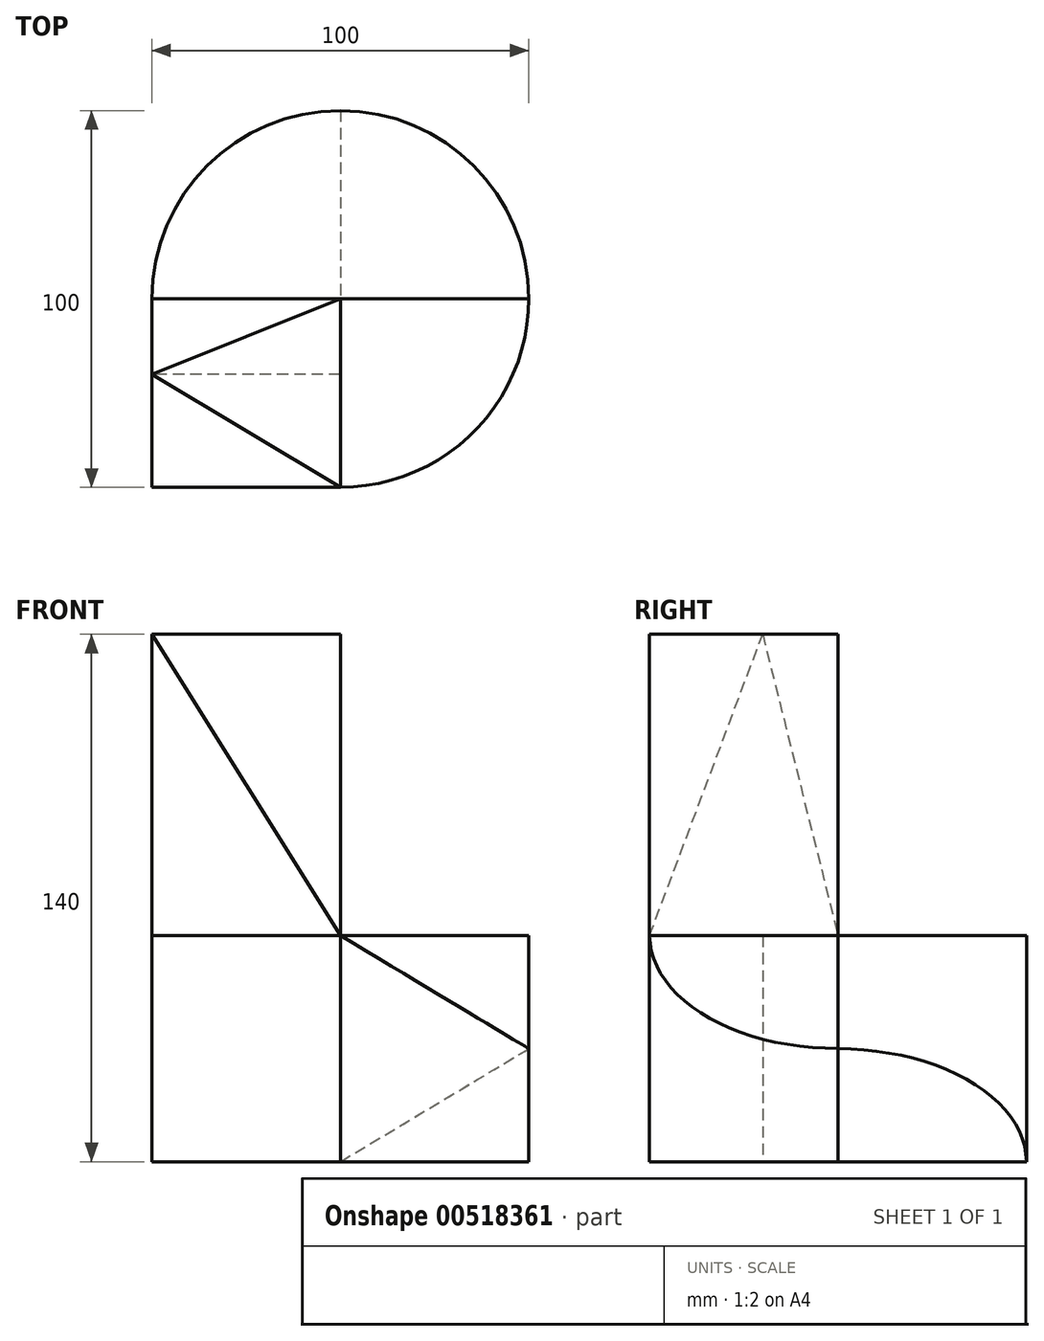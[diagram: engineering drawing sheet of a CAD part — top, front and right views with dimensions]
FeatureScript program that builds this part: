
annotation { "Feature Type Name" : "Feature", "Feature Type Description" : "" }
export const myFeature = defineFeature(function(context is Context, id is Id, definition is map)
    precondition{}
    {
        {
            var Q0;
            Q0=qCreatedBy(makeId("Top.planeOp"),FACE);
            var sketch = newSketch(context, id + "F0", { "sketchPlane" : qUnion([Q0])});
            skLineSegment(sketch, "E0.bottom", {"start": v(0, 0) * mm, "end": v(100, 0) * mm});
            skLineSegment(sketch, "E0.top", {"start": v(0, 100) * mm, "end": v(100, 100) * mm});
            skLineSegment(sketch, "E0.left", {"start": v(0, 0) * mm, "end": v(0, 100) * mm});
            skLineSegment(sketch, "E0.right", {"start": v(100, 0) * mm, "end": v(100, 100) * mm});
            skSolve(sketch);
        }
        {
            var Q0;
            Q0 = qSketchRegion(id + "F0", true);
            extrude(context, id + "F1", {"entities" : qUnion([Q0]), "depth" : 140 * mm, "offsetDistance" : 25 * mm});
        }
        {
            var Q0;
            Q0=makeQuery(id+"F1.opExtrude","CAP_FACE",FACE,{"disambiguationData":[OSD([sQuery(id+"F0.wireOp",EDGE,"E0.bottom"),sQuery(id+"F0.wireOp",EDGE,"E0.top"),sQuery(id+"F0.wireOp",EDGE,"E0.left"),sQuery(id+"F0.wireOp",EDGE,"E0.right")])],"isStart":false});
            var sketch = newSketch(context, id + "F2", { "sketchPlane" : qUnion([Q0])});
            skCircle(sketch, "E1", {"center": v(50, 50) * mm, "radius": 50 * mm});
            skSolve(sketch);
        }
        {
            var Q0;
            {var subQ0=sQuery(id+"F2.wireOp",EDGE,"E1");var subQ1=makeQuery(id+"F1.opExtrude","CAP_EDGE",EDGE,{"disambiguationData":[OSD([sQuery(id+"F0.wireOp",EDGE,"E0.top")])],"isStart":false});var subQ2=makeQuery(id+"F2.imprint","INTERSECT",VERTEX,{"derivedFrom":[subQ1,subQ0]});Q0=makeQuery(id+"F2.imprint","IMPRINT",FACE,{"disambiguationData":[TD([[makeQuery(id+"F2.imprint","IMPRINT",EDGE,{"disambiguationData":[TD([[subQ2,-1.0]])],"derivedFrom":subQ0}),-1.0]])]});}
            var Q1;
            {var subQ0=sQuery(id+"F2.wireOp",EDGE,"E1");var subQ1=makeQuery(id+"F1.opExtrude","CAP_EDGE",EDGE,{"disambiguationData":[OSD([sQuery(id+"F0.wireOp",EDGE,"E0.top")])],"isStart":false});var subQ2=makeQuery(id+"F2.imprint","INTERSECT",VERTEX,{"derivedFrom":[subQ1,subQ0]});Q1=makeQuery(id+"F2.imprint","IMPRINT",FACE,{"disambiguationData":[TD([[makeQuery(id+"F2.imprint","IMPRINT",EDGE,{"disambiguationData":[TD([[subQ2,1.0]])],"derivedFrom":subQ0}),-1.0]])]});}
            var Q2;
            {var subQ0=sQuery(id+"F2.wireOp",EDGE,"E1");var subQ1=makeQuery(id+"F1.opExtrude","CAP_EDGE",EDGE,{"disambiguationData":[OSD([sQuery(id+"F0.wireOp",EDGE,"E0.right")])],"isStart":false});var subQ2=makeQuery(id+"F2.imprint","INTERSECT",VERTEX,{"derivedFrom":[subQ1,subQ0]});Q2=makeQuery(id+"F2.imprint","IMPRINT",FACE,{"disambiguationData":[TD([[makeQuery(id+"F2.imprint","IMPRINT",EDGE,{"disambiguationData":[TD([[subQ2,1.0]])],"derivedFrom":subQ0}),-1.0]])]});}
            extrude(context, id + "F3", {"entities" : qUnion([Q0, Q1, Q2]), "operationType" : NewBodyOperationType.REMOVE, "endBound" : BoundingType.THROUGH_ALL, "oppositeDirection" : true, "depth" : 25 * mm, "offsetDistance" : 25 * mm});
        }
        {
            var Q0;
            Q0=makeQuery(id+"F1.opExtrude","CAP_FACE",FACE,{"disambiguationData":[OSD([sQuery(id+"F0.wireOp",EDGE,"E0.bottom"),sQuery(id+"F0.wireOp",EDGE,"E0.top"),sQuery(id+"F0.wireOp",EDGE,"E0.left"),sQuery(id+"F0.wireOp",EDGE,"E0.right")])],"isStart":false});
            var sketch = newSketch(context, id + "F4", { "sketchPlane" : qUnion([Q0])});
            skLineSegment(sketch, "E2", {"start": v(0, 50) * mm, "end": v(50, 50) * mm});
            skLineSegment(sketch, "E3", {"start": v(50, 50) * mm, "end": v(50, 0) * mm});
            skSolve(sketch);
        }
        {
            var Q0;
            Q0=makeQuery(id+"F4.imprint","IMPRINT",FACE,{"disambiguationData":[TD([[makeQuery(id+"F4.imprint","IMPRINT",EDGE,{"derivedFrom":sQuery(id+"F4.wireOp",EDGE,"E2")}),1.0]])]});
            extrude(context, id + "F5", {"entities" : qUnion([Q0]), "operationType" : NewBodyOperationType.REMOVE, "oppositeDirection" : true, "depth" : 80 * mm, "offsetDistance" : 25 * mm});
        }
        {
            var Q0;
            Q0=makeQuery(id+"F1.opExtrude","SWEPT_FACE",FACE,{"disambiguationData":[OSD([sQuery(id+"F0.wireOp",EDGE,"E0.bottom")])]});
            var sketch = newSketch(context, id + "F6", { "sketchPlane" : qUnion([Q0])});
            skLineSegment(sketch, "E4", {"start": v(50, 60) * mm, "end": v(0, 60) * mm});
            skLineSegment(sketch, "E5", {"start": v(0, 60) * mm, "end": v(0, 140) * mm});
            skLineSegment(sketch, "E6", {"start": v(0, 140) * mm, "end": v(50, 140) * mm});
            skLineSegment(sketch, "E7", {"start": v(50, 140) * mm, "end": v(50, 60) * mm});
            skSolve(sketch);
        }
        {
            var Q0;
            Q0=qCreatedBy(makeId("Front.planeOp"),FACE);
            var Q1;
            {var subQ0=sQuery(id+"F4.wireOp",EDGE,"E3");var subQ1=sQuery(id+"F4.wireOp",EDGE,"E2");var subQ2=makeQuery(id+"F5.boolean.opBoolean","COPY",VERTEX,{"derivedFrom":makeQuery(id+"F5.opExtrude","CAP_VERTEX",VERTEX,{"disambiguationData":[OSD([subQ1,subQ0])],"isStart":false})});Q1=makeQuery(id+"FeBywo4ubQIOEyD_1.boolean.opBoolean","MERGE",VERTEX,{"derivedFrom":[subQ2,makeQuery(id+"FeBywo4ubQIOEyD_1.opLoft","MID_CAP_VERTEX",VERTEX,{"disambiguationData":[OSD([subQ1,subQ0]),TDD([subQ2])],"capPos":0.0})]});}
            cPlane(context, id + "F7", {"entities" : qUnion([Q0, Q1]), "cplaneType" : CPlaneType.PLANE_POINT, "offset" : 25 * mm, "width" : 150 * mm, "height" : 150 * mm});
        }
        {
            var Q0;
            Q0=qCreatedBy(id+"F7.planeOp",FACE);
            var sketch = newSketch(context, id + "F8", { "sketchPlane" : qUnion([Q0])});
            skLineSegment(sketch, "E8", {"start": v(50, 60) * mm, "end": v(100, 60) * mm});
            skLineSegment(sketch, "E9", {"start": v(100, 60) * mm, "end": v(100, 30) * mm});
            skLineSegment(sketch, "E10", {"start": v(100, 30) * mm, "end": v(50, 60) * mm});
            skSolve(sketch);
        }
        {
            var Q0;
            Q0 = qSketchRegion(id + "F8", true);
            extrude(context, id + "F9", {"entities" : qUnion([Q0]), "operationType" : NewBodyOperationType.REMOVE, "endBound" : BoundingType.UP_TO_NEXT, "depth" : 25 * mm, "offsetDistance" : 25 * mm});
        }
        {
            var Q0;
            Q0=qCreatedBy(id+"F7.planeOp",FACE);
            var sketch = newSketch(context, id + "F10", { "sketchPlane" : qUnion([Q0])});
            skLineSegment(sketch, "E11", {"start": v(100, 0) * mm, "end": v(100, 29.99) * mm});
            skLineSegment(sketch, "E12", {"start": v(100, 29.99) * mm, "end": v(100, 0) * mm});
            skLineSegment(sketch, "E13", {"start": v(50, 0) * mm, "end": v(100, 30) * mm});
            skLineSegment(sketch, "E14", {"start": v(100, 0) * mm, "end": v(50, 0) * mm});
            skSolve(sketch);
        }
        {
            var Q0;
            Q0 = qSketchRegion(id + "F10", true);
            extrude(context, id + "F11", {"entities" : qUnion([Q0]), "operationType" : NewBodyOperationType.REMOVE, "endBound" : BoundingType.UP_TO_NEXT, "oppositeDirection" : true, "depth" : 25 * mm, "offsetDistance" : 25 * mm});
        }
        {
            var Q0;
            Q0=makeQuery(id+"F1.opExtrude","CAP_FACE",FACE,{"disambiguationData":[OSD([sQuery(id+"F0.wireOp",EDGE,"E0.bottom"),sQuery(id+"F0.wireOp",EDGE,"E0.top"),sQuery(id+"F0.wireOp",EDGE,"E0.left"),sQuery(id+"F0.wireOp",EDGE,"E0.right")])],"isStart":false});
            var sketch = newSketch(context, id + "F12", { "sketchPlane" : qUnion([Q0])});
            skLineSegment(sketch, "E15", {"start": v(50, 50) * mm, "end": v(0, 30) * mm});
            skLineSegment(sketch, "E16", {"start": v(0, 30) * mm, "end": v(50, 0) * mm});
            skLineSegment(sketch, "E17", {"start": v(50, 0) * mm, "end": v(50, 50) * mm});
            skSolve(sketch);
        }
        {
            var Q1;
            Q1=makeQuery(id+"F6.imprint","IMPRINT",FACE,{"disambiguationData":[TD([[makeQuery(id+"F6.imprint","IMPRINT",EDGE,{"derivedFrom":sQuery(id+"F6.wireOp",EDGE,"E4")}),-1.0]])]});
            var Q2;
            Q2=sQuery(id+"F12.wireOp",VERTEX,"E16.start");
            loft(context, id + "F13", {"operationType" : NewBodyOperationType.REMOVE, "sheetProfilesArray" : [{ "sheetProfileEntities" : qUnion([Q1]) }, { "sheetProfileEntities" : qUnion([Q2]) }]});
        }
        {
            var Q0;
            Q0=makeQuery(id+"F1.opExtrude","SWEPT_FACE",FACE,{"disambiguationData":[OSD([sQuery(id+"F0.wireOp",EDGE,"E0.left")])]});
            var sketch = newSketch(context, id + "F14", { "sketchPlane" : qUnion([Q0])});
            skLineSegment(sketch, "E18", {"start": v(-30, 140) * mm, "end": v(-30, 0) * mm});
            skLineSegment(sketch, "E19", {"start": v(-30, 0) * mm, "end": v(-50, 0) * mm});
            skLineSegment(sketch, "E20", {"start": v(-50, 0) * mm, "end": v(-50, 60) * mm});
            skLineSegment(sketch, "E21", {"start": v(-50, 60) * mm, "end": v(0, 60) * mm});
            skLineSegment(sketch, "E22", {"start": v(0, 60) * mm, "end": v(0, 0) * mm});
            skLineSegment(sketch, "E23", {"start": v(0, 0) * mm, "end": v(-30, 0) * mm});
            skSolve(sketch);
        }
        {
            var Q0;
            Q0=makeQuery(id+"F1.opExtrude","CAP_FACE",FACE,{"disambiguationData":[OSD([sQuery(id+"F0.wireOp",EDGE,"E0.bottom"),sQuery(id+"F0.wireOp",EDGE,"E0.top"),sQuery(id+"F0.wireOp",EDGE,"E0.left"),sQuery(id+"F0.wireOp",EDGE,"E0.right")])],"isStart":true});
            var sketch = newSketch(context, id + "F15", { "sketchPlane" : qUnion([Q0])});
            skLineSegment(sketch, "E24", {"start": v(0, -30) * mm, "end": v(50, 0) * mm});
            skSolve(sketch);
        }
        {
            var Q0;
            {var subQ4=sQuery(id+"F14.wireOp",EDGE,"E22");Q0=makeQuery(id+"F14.imprint","IMPRINT",FACE,{"disambiguationData":[TD([[makeQuery(id+"F14.imprint","IMPRINT",EDGE,{"derivedFrom":subQ4}),-1.0]])]});}
            extrude(context, id + "F16", {"entities" : qUnion([Q0]), "operationType" : NewBodyOperationType.REMOVE, "oppositeDirection" : true, "depth" : 50 * mm, "offsetDistance" : 25 * mm});
        }
        {
            var Q0;
            Q0=makeQuery(id+"F1.opExtrude","CAP_FACE",FACE,{"disambiguationData":[OSD([sQuery(id+"F0.wireOp",EDGE,"E0.bottom"),sQuery(id+"F0.wireOp",EDGE,"E0.top"),sQuery(id+"F0.wireOp",EDGE,"E0.left"),sQuery(id+"F0.wireOp",EDGE,"E0.right")])],"isStart":false});
            var sketch = newSketch(context, id + "F17", { "sketchPlane" : qUnion([Q0])});
            skLineSegment(sketch, "E25", {"start": v(0, 30) * mm, "end": v(0, 50) * mm});
            skLineSegment(sketch, "E26", {"start": v(0, 50) * mm, "end": v(50, 50) * mm});
            skLineSegment(sketch, "E27", {"start": v(50, 50) * mm, "end": v(0, 30) * mm});
            skSolve(sketch);
        }
        {
            var Q1;
            Q1=makeQuery(id+"F17.imprint","IMPRINT",FACE,{"disambiguationData":[TD([[makeQuery(id+"F17.imprint","IMPRINT",EDGE,{"derivedFrom":sQuery(id+"F17.wireOp",EDGE,"E25")}),-1.0]])]});
            var Q2;
            Q2=makeQuery(id+"F5.boolean.opBoolean","COPY",VERTEX,{"derivedFrom":makeQuery(id+"F5.opExtrude","CAP_VERTEX",VERTEX,{"disambiguationData":[OSD([sQuery(id+"F4.wireOp",EDGE,"E2"),sQuery(id+"F4.wireOp",EDGE,"E3")])],"isStart":false})});
            loft(context, id + "F18", {"operationType" : NewBodyOperationType.REMOVE, "sheetProfilesArray" : [{ "sheetProfileEntities" : qUnion([Q1]) }, { "sheetProfileEntities" : qUnion([Q2]) }]});
        }
    });
